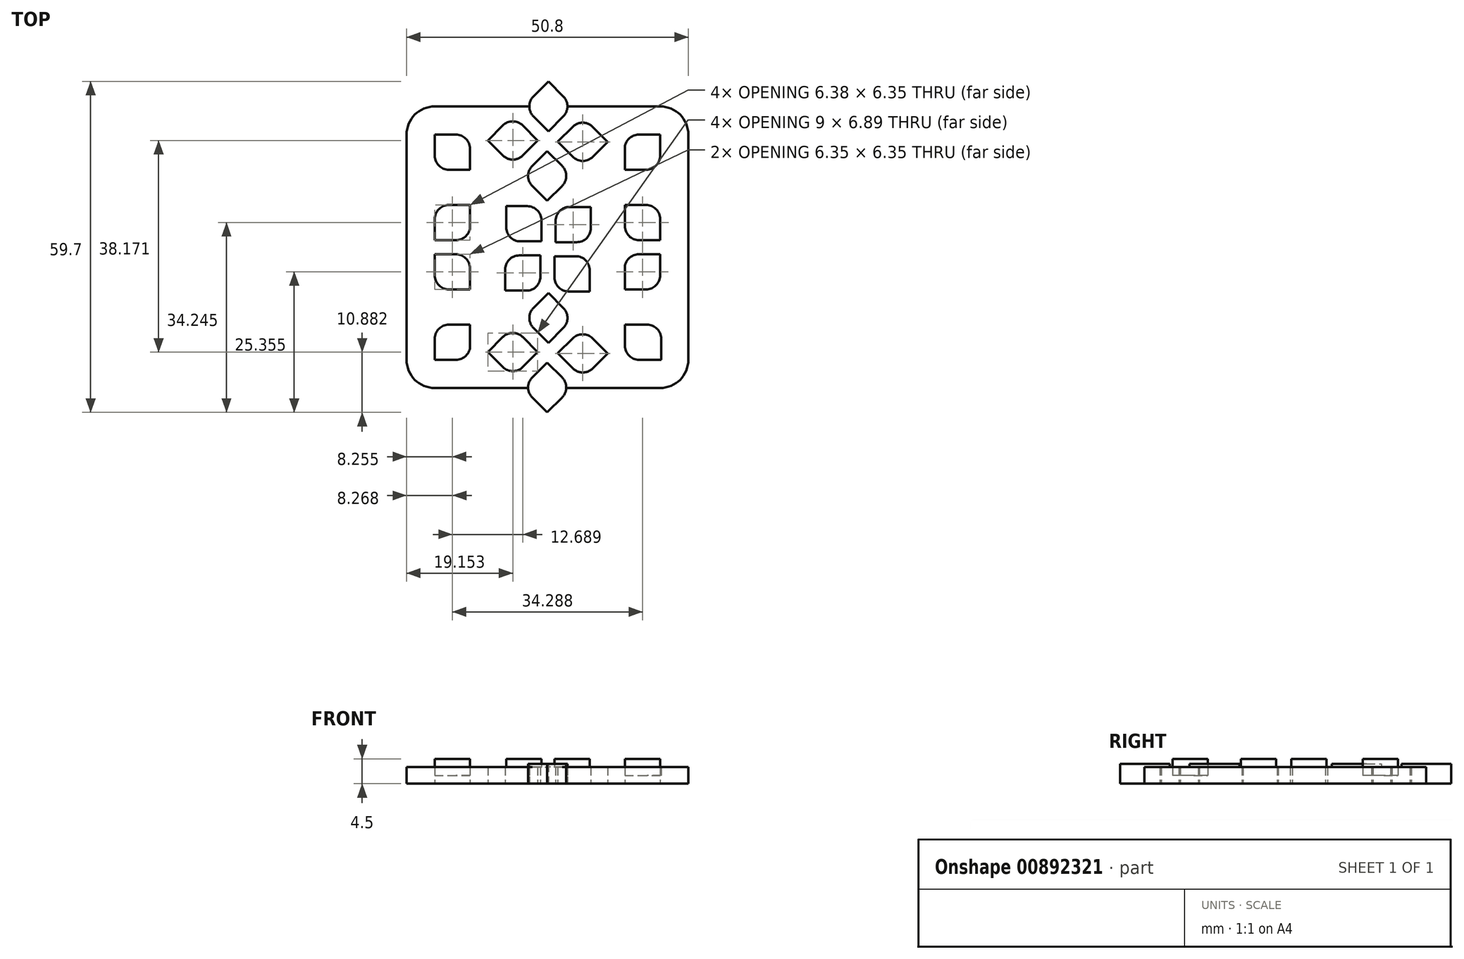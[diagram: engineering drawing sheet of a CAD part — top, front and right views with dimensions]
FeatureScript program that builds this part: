
annotation { "Feature Type Name" : "Feature", "Feature Type Description" : "" }
export const myFeature = defineFeature(function(context is Context, id is Id, definition is map)
    precondition{}
    {
        {
            var Q0;
            Q0=qCreatedBy(makeId("Top.planeOp"),FACE);
            var sketch = newSketch(context, id + "F0", { "sketchPlane" : qUnion([Q0])});
            skLineSegment(sketch, "E0.bottom", {"start": v(20.32, -25.4) * mm, "end": v(-20.32, -25.4) * mm});
            skLineSegment(sketch, "E0.top", {"start": v(20.32, 25.4) * mm, "end": v(-20.32, 25.4) * mm});
            skLineSegment(sketch, "E0.left", {"start": v(25.4, -20.32) * mm, "end": v(25.4, 20.32) * mm});
            skLineSegment(sketch, "E0.right", {"start": v(-25.4, -20.32) * mm, "end": v(-25.4, 20.32) * mm});
            skPoint(sketch, "E0.middle", {"position": v(0, 0) * mm});
            skPoint(sketch, "E1.visualSharp", {"position": v(-25.4, 25.4) * mm});
            skArc(sketch, "E1.filletArc", {"start": v(-20.32, 25.4) * mm, "mid": v(-23.91, 23.91) * mm, "end": v(-25.4, 20.32) * mm});
            skPoint(sketch, "E2.visualSharp", {"position": v(25.4, 25.4) * mm});
            skArc(sketch, "E2.filletArc", {"start": v(25.4, 20.32) * mm, "mid": v(23.91, 23.91) * mm, "end": v(20.32, 25.4) * mm});
            skPoint(sketch, "E3.visualSharp", {"position": v(25.4, -25.4) * mm});
            skArc(sketch, "E3.filletArc", {"start": v(20.32, -25.4) * mm, "mid": v(23.91, -23.91) * mm, "end": v(25.4, -20.32) * mm});
            skPoint(sketch, "E4.visualSharp", {"position": v(-25.4, -25.4) * mm});
            skArc(sketch, "E4.filletArc", {"start": v(-25.4, -20.32) * mm, "mid": v(-23.91, -23.91) * mm, "end": v(-20.32, -25.4) * mm});
            skLineSegment(sketch, "E5.bottom", {"start": v(20.32, 20.32) * mm, "end": v(16.48, 20.32) * mm});
            skLineSegment(sketch, "E5.top", {"start": v(17.78, 13.97) * mm, "end": v(13.94, 13.97) * mm});
            skLineSegment(sketch, "E5.left", {"start": v(20.32, 20.32) * mm, "end": v(20.32, 16.51) * mm});
            skLineSegment(sketch, "E5.right", {"start": v(13.94, 17.78) * mm, "end": v(13.94, 13.97) * mm});
            skLineSegment(sketch, "E6.bottom", {"start": v(-20.32, 20.32) * mm, "end": v(-16.51, 20.32) * mm});
            skLineSegment(sketch, "E6.top", {"start": v(-17.78, 13.97) * mm, "end": v(-13.97, 13.97) * mm});
            skLineSegment(sketch, "E6.left", {"start": v(-20.32, 20.32) * mm, "end": v(-20.32, 16.51) * mm});
            skLineSegment(sketch, "E6.right", {"start": v(-13.97, 17.78) * mm, "end": v(-13.97, 13.97) * mm});
            skPoint(sketch, "E7.visualSharp", {"position": v(-13.97, 20.32) * mm});
            skArc(sketch, "E7.filletArc", {"start": v(-13.97, 17.78) * mm, "mid": v(-14.71, 19.58) * mm, "end": v(-16.51, 20.32) * mm});
            skPoint(sketch, "E8.visualSharp", {"position": v(-20.32, 13.97) * mm});
            skArc(sketch, "E8.filletArc", {"start": v(-20.32, 16.51) * mm, "mid": v(-19.58, 14.71) * mm, "end": v(-17.78, 13.97) * mm});
            skPoint(sketch, "E9.visualSharp", {"position": v(13.94, 20.32) * mm});
            skArc(sketch, "E9.filletArc", {"start": v(16.48, 20.32) * mm, "mid": v(14.69, 19.58) * mm, "end": v(13.94, 17.78) * mm});
            skPoint(sketch, "E10.visualSharp", {"position": v(20.32, 13.97) * mm});
            skArc(sketch, "E10.filletArc", {"start": v(17.78, 13.97) * mm, "mid": v(19.58, 14.71) * mm, "end": v(20.32, 16.51) * mm});
            skLineSegment(sketch, "E11.bottom", {"start": v(-13.94, -13.97) * mm, "end": v(-17.78, -13.97) * mm});
            skLineSegment(sketch, "E11.top", {"start": v(-16.48, -20.32) * mm, "end": v(-20.32, -20.32) * mm});
            skLineSegment(sketch, "E11.left", {"start": v(-13.94, -13.97) * mm, "end": v(-13.94, -17.78) * mm});
            skLineSegment(sketch, "E11.right", {"start": v(-20.32, -16.51) * mm, "end": v(-20.32, -20.32) * mm});
            skArc(sketch, "E12.filletArc", {"start": v(-17.78, -13.97) * mm, "mid": v(-19.58, -14.71) * mm, "end": v(-20.32, -16.51) * mm});
            skArc(sketch, "E13.filletArc", {"start": v(-16.48, -20.32) * mm, "mid": v(-14.69, -19.58) * mm, "end": v(-13.94, -17.78) * mm});
            skLineSegment(sketch, "E14.bottom", {"start": v(13.97, -13.97) * mm, "end": v(17.95, -13.97) * mm});
            skLineSegment(sketch, "E14.top", {"start": v(16.51, -20.32) * mm, "end": v(20.5, -20.32) * mm});
            skLineSegment(sketch, "E14.left", {"start": v(13.97, -13.97) * mm, "end": v(13.97, -17.78) * mm});
            skLineSegment(sketch, "E14.right", {"start": v(20.5, -16.5) * mm, "end": v(20.5, -20.32) * mm});
            skArc(sketch, "E15.filletArc", {"start": v(20.5, -16.5) * mm, "mid": v(19.75, -14.71) * mm, "end": v(17.95, -13.97) * mm});
            skArc(sketch, "E16.filletArc", {"start": v(13.97, -17.78) * mm, "mid": v(14.71, -19.58) * mm, "end": v(16.51, -20.32) * mm});
            skLineSegment(sketch, "E17.bottom", {"start": v(13.97, 7.62) * mm, "end": v(17.78, 7.62) * mm});
            skLineSegment(sketch, "E17.top", {"start": v(16.5, 1.27) * mm, "end": v(20.32, 1.27) * mm});
            skLineSegment(sketch, "E17.left", {"start": v(13.97, 7.62) * mm, "end": v(13.97, 3.81) * mm});
            skLineSegment(sketch, "E17.right", {"start": v(20.32, 5.08) * mm, "end": v(20.32, 1.27) * mm});
            skArc(sketch, "E18.filletArc", {"start": v(20.32, 5.08) * mm, "mid": v(19.58, 6.88) * mm, "end": v(17.78, 7.62) * mm});
            skArc(sketch, "E19.filletArc", {"start": v(13.97, 3.81) * mm, "mid": v(14.71, 2.01) * mm, "end": v(16.5, 1.27) * mm});
            skLineSegment(sketch, "E20.bottom", {"start": v(20.32, -1.27) * mm, "end": v(16.48, -1.27) * mm});
            skLineSegment(sketch, "E20.top", {"start": v(17.78, -7.62) * mm, "end": v(13.94, -7.62) * mm});
            skLineSegment(sketch, "E20.left", {"start": v(20.32, -1.27) * mm, "end": v(20.32, -5.08) * mm});
            skLineSegment(sketch, "E20.right", {"start": v(13.94, -3.8) * mm, "end": v(13.94, -7.62) * mm});
            skArc(sketch, "E21.filletArc", {"start": v(16.48, -1.27) * mm, "mid": v(14.69, -2.01) * mm, "end": v(13.94, -3.8) * mm});
            skArc(sketch, "E22.filletArc", {"start": v(17.78, -7.62) * mm, "mid": v(19.58, -6.88) * mm, "end": v(20.32, -5.08) * mm});
            skLineSegment(sketch, "E23.bottom", {"start": v(-13.97, -7.62) * mm, "end": v(-17.78, -7.62) * mm});
            skLineSegment(sketch, "E23.top", {"start": v(-16.5, -1.27) * mm, "end": v(-20.32, -1.27) * mm});
            skLineSegment(sketch, "E23.left", {"start": v(-13.97, -7.62) * mm, "end": v(-13.97, -3.8) * mm});
            skLineSegment(sketch, "E23.right", {"start": v(-20.32, -5.08) * mm, "end": v(-20.32, -1.27) * mm});
            skArc(sketch, "E24.filletArc", {"start": v(-20.32, -5.08) * mm, "mid": v(-19.58, -6.88) * mm, "end": v(-17.78, -7.62) * mm});
            skArc(sketch, "E25.filletArc", {"start": v(-13.97, -3.8) * mm, "mid": v(-14.71, -2.01) * mm, "end": v(-16.5, -1.27) * mm});
            skLineSegment(sketch, "E26.bottom", {"start": v(-20.32, 1.27) * mm, "end": v(-16.48, 1.27) * mm});
            skLineSegment(sketch, "E26.top", {"start": v(-17.78, 7.62) * mm, "end": v(-13.94, 7.62) * mm});
            skLineSegment(sketch, "E26.left", {"start": v(-20.32, 1.27) * mm, "end": v(-20.32, 5.08) * mm});
            skLineSegment(sketch, "E26.right", {"start": v(-13.94, 3.8) * mm, "end": v(-13.94, 7.62) * mm});
            skArc(sketch, "E27.filletArc", {"start": v(-16.48, 1.27) * mm, "mid": v(-14.69, 2.01) * mm, "end": v(-13.94, 3.8) * mm});
            skArc(sketch, "E28.filletArc", {"start": v(-17.78, 7.62) * mm, "mid": v(-19.58, 6.88) * mm, "end": v(-20.32, 5.08) * mm});
            skLineSegment(sketch, "E29.bottom", {"start": v(-7.43, 7.4) * mm, "end": v(-3.62, 7.4) * mm});
            skLineSegment(sketch, "E29.top", {"start": v(-4.9, 1.05) * mm, "end": v(-1.08, 1.05) * mm});
            skLineSegment(sketch, "E29.left", {"start": v(-7.43, 7.4) * mm, "end": v(-7.43, 3.59) * mm});
            skLineSegment(sketch, "E29.right", {"start": v(-1.08, 4.86) * mm, "end": v(-1.08, 1.05) * mm});
            skArc(sketch, "E30.filletArc", {"start": v(-1.08, 4.86) * mm, "mid": v(-1.83, 6.65) * mm, "end": v(-3.62, 7.4) * mm});
            skArc(sketch, "E31.filletArc", {"start": v(-7.43, 3.59) * mm, "mid": v(-6.7, 1.8) * mm, "end": v(-4.9, 1.05) * mm});
            skLineSegment(sketch, "E32.bottom", {"start": v(-1.26, -1.5) * mm, "end": v(-5.1, -1.5) * mm});
            skLineSegment(sketch, "E32.top", {"start": v(-3.8, -7.84) * mm, "end": v(-7.63, -7.84) * mm});
            skLineSegment(sketch, "E32.left", {"start": v(-1.26, -1.5) * mm, "end": v(-1.26, -5.3) * mm});
            skLineSegment(sketch, "E32.right", {"start": v(-7.63, -4.03) * mm, "end": v(-7.63, -7.84) * mm});
            skArc(sketch, "E33.filletArc", {"start": v(-5.1, -1.5) * mm, "mid": v(-6.89, -2.24) * mm, "end": v(-7.63, -4.03) * mm});
            skArc(sketch, "E34.filletArc", {"start": v(-3.8, -7.84) * mm, "mid": v(-2, -7.1) * mm, "end": v(-1.26, -5.3) * mm});
            skLineSegment(sketch, "E35.bottom", {"start": v(7.63, -7.98) * mm, "end": v(3.82, -7.98) * mm});
            skLineSegment(sketch, "E35.top", {"start": v(5.1, -1.63) * mm, "end": v(1.28, -1.63) * mm});
            skLineSegment(sketch, "E35.left", {"start": v(7.63, -7.98) * mm, "end": v(7.63, -4.17) * mm});
            skLineSegment(sketch, "E35.right", {"start": v(1.28, -5.44) * mm, "end": v(1.28, -1.63) * mm});
            skArc(sketch, "E36.filletArc", {"start": v(1.28, -5.44) * mm, "mid": v(2.03, -7.24) * mm, "end": v(3.82, -7.98) * mm});
            skArc(sketch, "E37.filletArc", {"start": v(7.63, -4.17) * mm, "mid": v(6.9, -2.38) * mm, "end": v(5.1, -1.63) * mm});
            skLineSegment(sketch, "E38.bottom", {"start": v(1.46, 0.9) * mm, "end": v(5.3, 0.9) * mm});
            skLineSegment(sketch, "E38.top", {"start": v(4, 7.26) * mm, "end": v(7.83, 7.26) * mm});
            skLineSegment(sketch, "E38.left", {"start": v(1.46, 0.9) * mm, "end": v(1.46, 4.72) * mm});
            skLineSegment(sketch, "E38.right", {"start": v(7.83, 3.45) * mm, "end": v(7.83, 7.26) * mm});
            skArc(sketch, "E39.filletArc", {"start": v(5.3, 0.9) * mm, "mid": v(7.09, 1.65) * mm, "end": v(7.83, 3.45) * mm});
            skArc(sketch, "E40.filletArc", {"start": v(4, 7.26) * mm, "mid": v(2.2, 6.51) * mm, "end": v(1.46, 4.72) * mm});
            skPoint(sketch, "E41.middle", {"position": v(0.2, 19.41) * mm});
            skLineSegment(sketch, "E42.bottom", {"start": v(0.17, 29.9) * mm, "end": v(2.86, 27.2) * mm});
            skLineSegment(sketch, "E42.top", {"start": v(-2.53, 23.61) * mm, "end": v(0.17, 20.92) * mm});
            skLineSegment(sketch, "E42.left", {"start": v(0.17, 29.9) * mm, "end": v(-2.53, 27.2) * mm});
            skLineSegment(sketch, "E42.right", {"start": v(2.86, 23.61) * mm, "end": v(0.17, 20.92) * mm});
            skArc(sketch, "E43.filletArc", {"start": v(2.86, 23.61) * mm, "mid": v(3.6, 25.4) * mm, "end": v(2.86, 27.2) * mm});
            skArc(sketch, "E44.filletArc", {"start": v(-2.53, 27.2) * mm, "mid": v(-3.27, 25.4) * mm, "end": v(-2.53, 23.61) * mm});
            skLineSegment(sketch, "E45.bottom", {"start": v(-1.75, 19.24) * mm, "end": v(-4.46, 21.96) * mm});
            skLineSegment(sketch, "E45.top", {"start": v(-8.03, 16.55) * mm, "end": v(-10.75, 19.26) * mm});
            skLineSegment(sketch, "E45.left", {"start": v(-1.75, 19.24) * mm, "end": v(-4.44, 16.55) * mm});
            skLineSegment(sketch, "E45.right", {"start": v(-8.05, 21.96) * mm, "end": v(-10.75, 19.26) * mm});
            skArc(sketch, "E46.filletArc", {"start": v(-4.46, 21.96) * mm, "mid": v(-6.26, 22.7) * mm, "end": v(-8.05, 21.96) * mm});
            skArc(sketch, "E47.filletArc", {"start": v(-8.03, 16.55) * mm, "mid": v(-6.24, 15.8) * mm, "end": v(-4.44, 16.55) * mm});
            skLineSegment(sketch, "E48.bottom", {"start": v(-0.05, 8.37) * mm, "end": v(-2.75, 11.06) * mm});
            skLineSegment(sketch, "E48.top", {"start": v(2.64, 14.65) * mm, "end": v(-0.05, 17.35) * mm});
            skLineSegment(sketch, "E48.left", {"start": v(-0.05, 8.37) * mm, "end": v(2.64, 11.06) * mm});
            skLineSegment(sketch, "E48.right", {"start": v(-2.75, 14.65) * mm, "end": v(-0.05, 17.35) * mm});
            skArc(sketch, "E49.filletArc", {"start": v(-2.75, 14.65) * mm, "mid": v(-3.49, 12.86) * mm, "end": v(-2.75, 11.06) * mm});
            skArc(sketch, "E50.filletArc", {"start": v(2.64, 11.06) * mm, "mid": v(3.39, 12.86) * mm, "end": v(2.64, 14.65) * mm});
            skLineSegment(sketch, "E51.bottom", {"start": v(1.87, 19.02) * mm, "end": v(4.58, 16.31) * mm});
            skLineSegment(sketch, "E51.top", {"start": v(8.15, 21.72) * mm, "end": v(10.86, 19) * mm});
            skLineSegment(sketch, "E51.left", {"start": v(1.87, 19.02) * mm, "end": v(4.56, 21.72) * mm});
            skLineSegment(sketch, "E51.right", {"start": v(8.17, 16.31) * mm, "end": v(10.86, 19) * mm});
            skArc(sketch, "E52.filletArc", {"start": v(4.58, 16.31) * mm, "mid": v(6.37, 15.57) * mm, "end": v(8.17, 16.31) * mm});
            skArc(sketch, "E53.filletArc", {"start": v(8.15, 21.72) * mm, "mid": v(6.36, 22.46) * mm, "end": v(4.56, 21.72) * mm});
            skPoint(sketch, "E54.middle", {"position": v(0.2, -18.76) * mm});
            skLineSegment(sketch, "E55.bottom", {"start": v(0.17, -8.27) * mm, "end": v(2.86, -10.97) * mm});
            skLineSegment(sketch, "E55.top", {"start": v(-2.53, -14.56) * mm, "end": v(0.17, -17.25) * mm});
            skLineSegment(sketch, "E55.left", {"start": v(0.17, -8.27) * mm, "end": v(-2.53, -10.97) * mm});
            skLineSegment(sketch, "E55.right", {"start": v(2.86, -14.56) * mm, "end": v(0.17, -17.25) * mm});
            skArc(sketch, "E56.filletArc", {"start": v(2.86, -14.56) * mm, "mid": v(3.6, -12.76) * mm, "end": v(2.86, -10.97) * mm});
            skArc(sketch, "E57.filletArc", {"start": v(-2.53, -10.97) * mm, "mid": v(-3.27, -12.76) * mm, "end": v(-2.53, -14.56) * mm});
            skLineSegment(sketch, "E58.bottom", {"start": v(-1.75, -18.93) * mm, "end": v(-4.46, -16.22) * mm});
            skLineSegment(sketch, "E58.top", {"start": v(-8.03, -21.62) * mm, "end": v(-10.75, -18.9) * mm});
            skLineSegment(sketch, "E58.left", {"start": v(-1.75, -18.93) * mm, "end": v(-4.44, -21.62) * mm});
            skLineSegment(sketch, "E58.right", {"start": v(-8.05, -16.22) * mm, "end": v(-10.75, -18.9) * mm});
            skArc(sketch, "E59.filletArc", {"start": v(-4.46, -16.22) * mm, "mid": v(-6.26, -15.47) * mm, "end": v(-8.05, -16.22) * mm});
            skArc(sketch, "E60.filletArc", {"start": v(-8.03, -21.62) * mm, "mid": v(-6.24, -22.37) * mm, "end": v(-4.44, -21.62) * mm});
            skLineSegment(sketch, "E61.bottom", {"start": v(-0.05, -29.8) * mm, "end": v(-2.75, -27.1) * mm});
            skLineSegment(sketch, "E61.top", {"start": v(2.64, -23.52) * mm, "end": v(-0.05, -20.82) * mm});
            skLineSegment(sketch, "E61.left", {"start": v(-0.05, -29.8) * mm, "end": v(2.64, -27.1) * mm});
            skLineSegment(sketch, "E61.right", {"start": v(-2.75, -23.52) * mm, "end": v(-0.05, -20.82) * mm});
            skArc(sketch, "E62.filletArc", {"start": v(-2.75, -23.52) * mm, "mid": v(-3.49, -25.31) * mm, "end": v(-2.75, -27.1) * mm});
            skArc(sketch, "E63.filletArc", {"start": v(2.64, -27.1) * mm, "mid": v(3.39, -25.31) * mm, "end": v(2.64, -23.52) * mm});
            skLineSegment(sketch, "E64.bottom", {"start": v(1.87, -19.15) * mm, "end": v(4.58, -21.86) * mm});
            skLineSegment(sketch, "E64.top", {"start": v(8.15, -16.45) * mm, "end": v(10.86, -19.17) * mm});
            skLineSegment(sketch, "E64.left", {"start": v(1.87, -19.15) * mm, "end": v(4.56, -16.45) * mm});
            skLineSegment(sketch, "E64.right", {"start": v(8.17, -21.86) * mm, "end": v(10.86, -19.17) * mm});
            skArc(sketch, "E65.filletArc", {"start": v(4.58, -21.86) * mm, "mid": v(6.37, -22.6) * mm, "end": v(8.17, -21.86) * mm});
            skArc(sketch, "E66.filletArc", {"start": v(8.15, -16.45) * mm, "mid": v(6.36, -15.7) * mm, "end": v(4.56, -16.45) * mm});
            skPoint(sketch, "E67", {"position": v(-3.27, 25.4) * mm});
            skSolve(sketch);
        }
        {
            var Q0;
            Q0=makeQuery(id+"F0.imprint","IMPRINT",FACE,{"disambiguationData":[TD([[makeQuery(id+"F0.imprint","IMPRINT",EDGE,{"derivedFrom":sQuery(id+"F0.wireOp",EDGE,"E0.left")}),1.0]])]});
            extrude(context, id + "F1", {"entities" : qUnion([Q0]), "depth" : 3 * mm, "offsetDistance" : 25.4 * mm});
        }
        {
            var Q0;
            {var subQ2=sQuery(id+"F0.wireOp",EDGE,"E42.bottom");Q0=makeQuery(id+"F0.imprint","IMPRINT",FACE,{"disambiguationData":[TD([[makeQuery(id+"F0.imprint","IMPRINT",EDGE,{"derivedFrom":subQ2}),-1.0]])]});}
            var Q1;
            {var subQ4=sQuery(id+"F0.wireOp",EDGE,"E42.top");Q1=makeQuery(id+"F0.imprint","IMPRINT",FACE,{"disambiguationData":[TD([[makeQuery(id+"F0.imprint","IMPRINT",EDGE,{"derivedFrom":subQ4}),1.0]])]});}
            var Q2;
            Q2=makeQuery(id+"F0.imprint","IMPRINT",FACE,{"disambiguationData":[TD([[makeQuery(id+"F0.imprint","IMPRINT",EDGE,{"derivedFrom":sQuery(id+"F0.wireOp",EDGE,"E48.bottom")}),-1.0]])]});
            var Q3;
            {var subQ2=sQuery(id+"F0.wireOp",EDGE,"E61.bottom");Q3=makeQuery(id+"F0.imprint","IMPRINT",FACE,{"disambiguationData":[TD([[makeQuery(id+"F0.imprint","IMPRINT",EDGE,{"derivedFrom":subQ2}),-1.0]])]});}
            var Q4;
            {var subQ1=sQuery(id+"F0.wireOp",EDGE,"E61.top");Q4=makeQuery(id+"F0.imprint","IMPRINT",FACE,{"disambiguationData":[TD([[makeQuery(id+"F0.imprint","IMPRINT",EDGE,{"derivedFrom":subQ1}),1.0]])]});}
            var Q5;
            Q5=makeQuery(id+"F0.imprint","IMPRINT",FACE,{"disambiguationData":[TD([[makeQuery(id+"F0.imprint","IMPRINT",EDGE,{"derivedFrom":sQuery(id+"F0.wireOp",EDGE,"E55.bottom")}),-1.0]])]});
            var Q6;
            Q6=sQuery(id+"F0.wireOp",EDGE,"E42.left");
            extrude(context, id + "F2", {"entities" : qUnion([Q0, Q1, Q2, Q3, Q4, Q5]), "operationType" : NewBodyOperationType.ADD, "surfaceEntities" : qUnion([Q6]), "depth" : 3.6 * mm, "offsetDistance" : 25.4 * mm});
        }
        {
            var Q0;
            Q0=makeQuery(id+"F0.imprint","IMPRINT",FACE,{"disambiguationData":[TD([[makeQuery(id+"F0.imprint","IMPRINT",EDGE,{"derivedFrom":sQuery(id+"F0.wireOp",EDGE,"E6.bottom")}),-1.0]])]});
            var Q1;
            Q1=makeQuery(id+"F0.imprint","IMPRINT",FACE,{"disambiguationData":[TD([[makeQuery(id+"F0.imprint","IMPRINT",EDGE,{"derivedFrom":sQuery(id+"F0.wireOp",EDGE,"E14.bottom")}),-1.0]])]});
            extrude(context, id + "F3", {"entities" : qUnion([Q0, Q1]), "operationType" : NewBodyOperationType.ADD, "depth" : 1.5 * mm, "offsetDistance" : 25.4 * mm});
        }
        {
            var Q0;
            Q0=makeQuery(id+"F0.imprint","IMPRINT",FACE,{"disambiguationData":[TD([[makeQuery(id+"F0.imprint","IMPRINT",EDGE,{"derivedFrom":sQuery(id+"F0.wireOp",EDGE,"E5.bottom")}),1.0]])]});
            var Q1;
            Q1=makeQuery(id+"F0.imprint","IMPRINT",FACE,{"disambiguationData":[TD([[makeQuery(id+"F0.imprint","IMPRINT",EDGE,{"derivedFrom":sQuery(id+"F0.wireOp",EDGE,"E11.bottom")}),1.0]])]});
            var Q2;
            Q2=makeQuery(id+"F0.imprint","IMPRINT",FACE,{"disambiguationData":[TD([[makeQuery(id+"F0.imprint","IMPRINT",EDGE,{"derivedFrom":sQuery(id+"F0.wireOp",EDGE,"E29.bottom")}),-1.0]])]});
            var Q3;
            Q3=makeQuery(id+"F0.imprint","IMPRINT",FACE,{"disambiguationData":[TD([[makeQuery(id+"F0.imprint","IMPRINT",EDGE,{"derivedFrom":sQuery(id+"F0.wireOp",EDGE,"E35.bottom")}),-1.0]])]});
            extrude(context, id + "F4", {"entities" : qUnion([Q0, Q1, Q2, Q3]), "operationType" : NewBodyOperationType.ADD, "depth" : 4.5 * mm, "offsetDistance" : 25.4 * mm});
        }
    });
